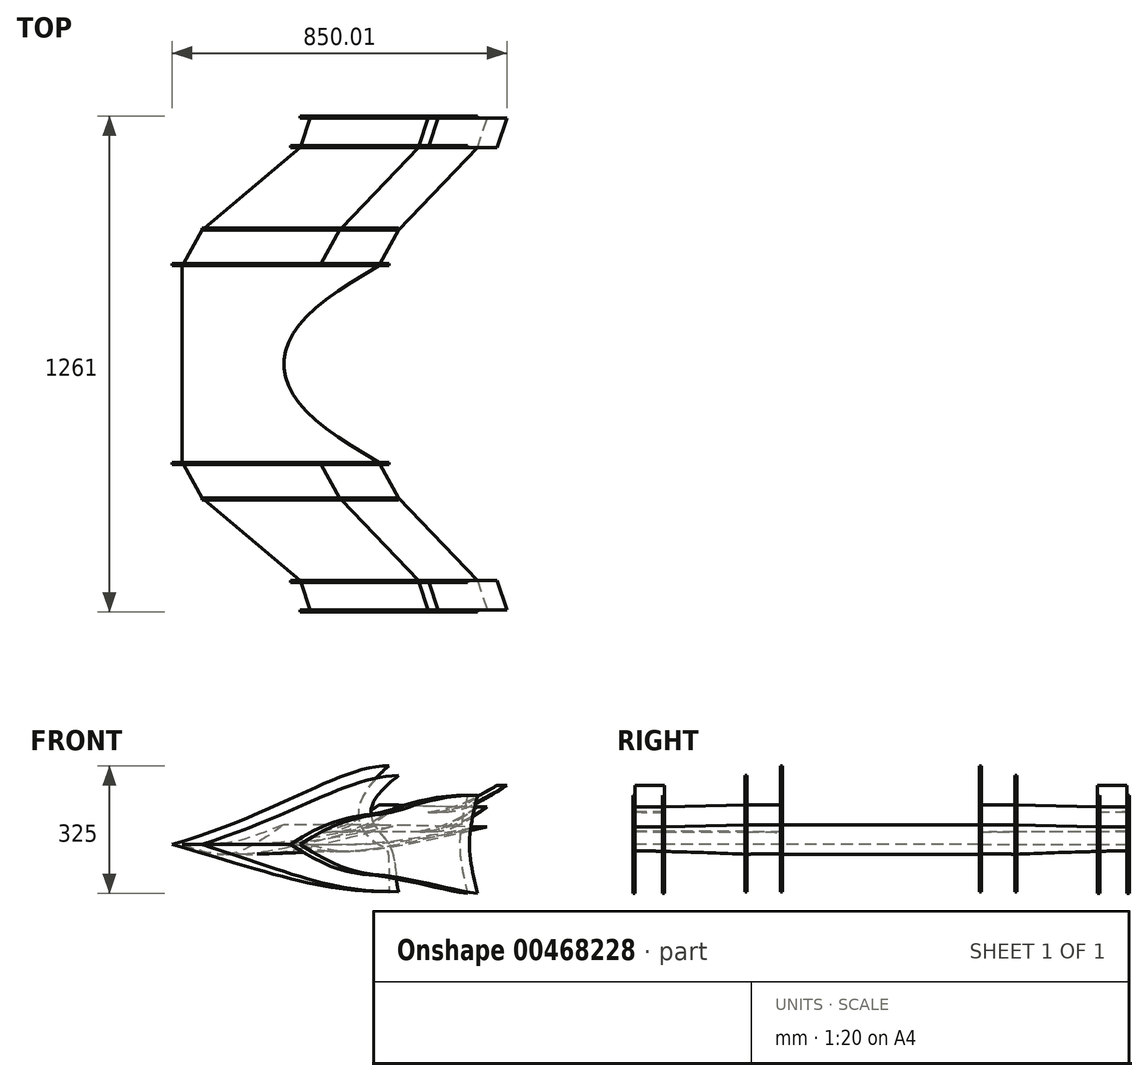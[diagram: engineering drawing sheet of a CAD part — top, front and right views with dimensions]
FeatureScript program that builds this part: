
annotation { "Feature Type Name" : "Feature", "Feature Type Description" : "" }
export const myFeature = defineFeature(function(context is Context, id is Id, definition is map)
    precondition{}
    {
        {
            var Q0;
            Q0=qCreatedBy(makeId("Right.planeOp"),FACE);
            cPlane(context, id + "F0", {"entities" : qUnion([Q0]), "cplaneType" : CPlaneType.OFFSET, "offset" : 250 * mm, "width" : 150 * mm, "height" : 150 * mm});
        }
        {
            var Q0;
            Q0=qCreatedBy(id+"F0.planeOp",FACE);
            var sketch = newSketch(context, id + "F1", { "sketchPlane" : qUnion([Q0])});
            skPoint(sketch, "E0.middle", {"position": v(0, 0) * mm});
            skFitSpline(sketch, "E1", {"points": [v(-275, 0) * mm, v(275, 200) * mm], "startDerivative": vector(825, 240) * mm, "endDerivative": vector(375, 0) * mm});
            skFitSpline(sketch, "E2", {"points": [v(275, 200) * mm, v(250, 0) * mm, v(275, -120) * mm], "startDerivative": vector(-734.18, -640.74) * mm, "endDerivative": vector(0, -821.63) * mm});
            skFitSpline(sketch, "E3", {"points": [v(-275, 0) * mm, v(275, -120) * mm], "startDerivative": vector(825, -240) * mm, "endDerivative": vector(525, 0) * mm});
            skSolve(sketch);
        }
        {
            var Q0;
            Q0=qCreatedBy(makeId("Right.planeOp"),FACE);
            cPlane(context, id + "F2", {"entities" : qUnion([Q0]), "cplaneType" : CPlaneType.OFFSET, "offset" : 340 * mm, "width" : 150 * mm, "height" : 150 * mm});
        }
        {
            var Q0;
            Q0=qCreatedBy(id+"F2.planeOp",FACE);
            var sketch = newSketch(context, id + "F3", { "sketchPlane" : qUnion([Q0])});
            skFitSpline(sketch, "E4", {"points": [v(-200, 0) * mm, v(300, 175) * mm], "startDerivative": vector(750, 240) * mm, "endDerivative": vector(375, 0) * mm});
            skFitSpline(sketch, "E5", {"points": [v(300, 175) * mm, v(275, 0) * mm, v(300, -120) * mm], "startDerivative": vector(-687.26, -522.32) * mm, "endDerivative": vector(77.93, -251.25) * mm});
            skFitSpline(sketch, "E6", {"points": [v(-200, 0) * mm, v(300, -120) * mm], "startDerivative": vector(750, -240) * mm, "endDerivative": vector(525, 0) * mm});
            skSolve(sketch);
        }
        {
            var Q0;
            Q0=qCreatedBy(makeId("Right.planeOp"),FACE);
            cPlane(context, id + "F4", {"entities" : qUnion([Q0]), "cplaneType" : CPlaneType.OFFSET, "offset" : 550 * mm, "width" : 150 * mm, "height" : 150 * mm});
        }
        {
            var Q0;
            Q0=qCreatedBy(id+"F4.planeOp",FACE);
            var sketch = newSketch(context, id + "F5", { "sketchPlane" : qUnion([Q0])});
            skFitSpline(sketch, "E7", {"points": [v(25, 0) * mm, v(250, 80) * mm, v(475, 125) * mm], "startDerivative": vector(742.6, 475.26) * mm, "endDerivative": vector(681.8, 0) * mm});
            skFitSpline(sketch, "E8", {"points": [v(475, 125) * mm, v(455, 0) * mm, v(475, -125) * mm], "startDerivative": vector(-60, -250) * mm, "endDerivative": vector(60, -250) * mm});
            skFitSpline(sketch, "E9", {"points": [v(25, 0) * mm, v(250, -80) * mm, v(475, -125) * mm], "startDerivative": vector(742.6, -475.26) * mm, "endDerivative": vector(456.76, -74.2) * mm});
            skSolve(sketch);
        }
        {
            var Q0;
            Q0=qCreatedBy(makeId("Right.planeOp"),FACE);
            cPlane(context, id + "F6", {"entities" : qUnion([Q0]), "cplaneType" : CPlaneType.OFFSET, "offset" : 625 * mm, "width" : 150 * mm, "height" : 150 * mm});
        }
        {
            var Q0;
            Q0=qCreatedBy(id+"F6.planeOp",FACE);
            var sketch = newSketch(context, id + "F7", { "sketchPlane" : qUnion([Q0])});
            skFitSpline(sketch, "E10", {"points": [v(50, 0) * mm, v(275, 80) * mm, v(500, 125) * mm], "startDerivative": vector(742.6, 475.26) * mm, "endDerivative": vector(681.8, 0) * mm});
            skFitSpline(sketch, "E11", {"points": [v(500, 125) * mm, v(480, 0) * mm, v(500, -125) * mm], "startDerivative": vector(-60, -250) * mm, "endDerivative": vector(60, -250) * mm});
            skFitSpline(sketch, "E12", {"points": [v(50, 0) * mm, v(275, -80) * mm, v(500, -125) * mm], "startDerivative": vector(742.6, -475.26) * mm, "endDerivative": vector(456.76, -74.2) * mm});
            skSolve(sketch);
        }
        {
            var Q0;
            Q0=qCreatedBy(makeId("Right.planeOp"),FACE);
            cPlane(context, id + "F8", {"entities" : qUnion([Q0]), "cplaneType" : CPlaneType.OFFSET, "offset" : 160 * mm, "width" : 150 * mm, "height" : 150 * mm});
        }
        {
            var Q0;
            Q0=qCreatedBy(id+"F8.planeOp",FACE);
            var sketch = newSketch(context, id + "F9", { "sketchPlane" : qUnion([Q0])});
            skFitSpline(sketch, "E13", {"points": [v(-250, 0) * mm, v(-125, -25) * mm, v(110, 50) * mm], "startDerivative": vector(276.92, -99.23) * mm, "endDerivative": vector(434.5, 183.8) * mm});
            skFitSpline(sketch, "E14", {"points": [v(-250, 0) * mm, v(110, 50) * mm], "startDerivative": vector(540, 0) * mm, "endDerivative": vector(540, 150) * mm});
            skSolve(sketch);
        }
        {
            var Q0;
            Q0=qCreatedBy(makeId("Right.planeOp"),FACE);
            cPlane(context, id + "F10", {"entities" : qUnion([Q0]), "cplaneType" : CPlaneType.OFFSET, "offset" : 250 * mm, "width" : 150 * mm, "height" : 150 * mm});
        }
        {
            var Q0;
            Q0=qCreatedBy(id+"F10.planeOp",FACE);
            var sketch = newSketch(context, id + "F11", { "sketchPlane" : qUnion([Q0])});
            skFitSpline(sketch, "E15", {"points": [v(-250, 0) * mm, v(-125, -25) * mm, v(250, 50) * mm], "startDerivative": vector(295.75, -102.45) * mm, "endDerivative": vector(670.75, 177.45) * mm});
            skFitSpline(sketch, "E16", {"points": [v(-250, 0) * mm, v(250, 50) * mm], "startDerivative": vector(750, 0) * mm, "endDerivative": vector(750, 150) * mm});
            skSolve(sketch);
        }
        {
            var Q0;
            Q0=qCreatedBy(id+"F10.planeOp",FACE);
            var sketch = newSketch(context, id + "F12", { "sketchPlane" : qUnion([Q0])});
            skFitSpline(sketch, "E17", {"points": [v(100, 32) * mm, v(125, 32) * mm, v(250, 100) * mm], "startDerivative": vector(70.95, -14.25) * mm, "endDerivative": vector(319.3, 251.19) * mm});
            skFitSpline(sketch, "E18", {"points": [v(100, 32) * mm, v(250, 100) * mm], "startDerivative": vector(225, 54) * mm, "endDerivative": vector(225, 150) * mm});
            skSolve(sketch);
        }
        {
            var Q0;
            Q0=qCreatedBy(makeId("Right.planeOp"),FACE);
            cPlane(context, id + "F13", {"entities" : qUnion([Q0]), "cplaneType" : CPlaneType.OFFSET, "offset" : 340 * mm, "width" : 150 * mm, "height" : 150 * mm});
        }
        {
            var Q0;
            Q0=qCreatedBy(id+"F13.planeOp",FACE);
            var sketch = newSketch(context, id + "F14", { "sketchPlane" : qUnion([Q0])});
            skFitSpline(sketch, "E19", {"points": [v(-200, 0) * mm, v(-75, -25) * mm, v(300, 50) * mm], "startDerivative": vector(295.75, -102.45) * mm, "endDerivative": vector(670.75, 177.45) * mm});
            skFitSpline(sketch, "E20", {"points": [v(-200, 0) * mm, v(300, 50) * mm], "startDerivative": vector(750, 0) * mm, "endDerivative": vector(750, 150) * mm});
            skSolve(sketch);
        }
        {
            var Q0;
            Q0=qCreatedBy(id+"F13.planeOp",FACE);
            var sketch = newSketch(context, id + "F15", { "sketchPlane" : qUnion([Q0])});
            skFitSpline(sketch, "E21", {"points": [v(150, 32.5) * mm, v(175, 32.5) * mm, v(300, 100) * mm], "startDerivative": vector(70.88, -14.16) * mm, "endDerivative": vector(319.39, 250.19) * mm});
            skFitSpline(sketch, "E22", {"points": [v(150, 32.5) * mm, v(300, 100) * mm], "startDerivative": vector(225, 52.5) * mm, "endDerivative": vector(225, 150) * mm});
            skSolve(sketch);
        }
        {
            var Q0;
            Q0=qCreatedBy(makeId("Right.planeOp"),FACE);
            cPlane(context, id + "F16", {"entities" : qUnion([Q0]), "cplaneType" : CPlaneType.OFFSET, "offset" : 550 * mm, "width" : 150 * mm, "height" : 150 * mm});
        }
        {
            var Q0;
            Q0=qCreatedBy(id+"F16.planeOp",FACE);
            var sketch = newSketch(context, id + "F17", { "sketchPlane" : qUnion([Q0])});
            skFitSpline(sketch, "E23", {"points": [v(50, 0) * mm, v(150, -18) * mm, v(500, 45) * mm], "startDerivative": vector(243.54, -77.51) * mm, "endDerivative": vector(618.54, 145.01) * mm});
            skFitSpline(sketch, "E24", {"points": [v(50, 0) * mm, v(500, 45) * mm], "startDerivative": vector(600, 0) * mm, "endDerivative": vector(750, 135) * mm});
            skSolve(sketch);
        }
        {
            var Q0;
            Q0=qCreatedBy(id+"F16.planeOp",FACE);
            var sketch = newSketch(context, id + "F18", { "sketchPlane" : qUnion([Q0])});
            skFitSpline(sketch, "E25", {"points": [v(350, 33) * mm, v(375, 33) * mm, v(500, 95) * mm], "startDerivative": vector(70.1, -13.12) * mm, "endDerivative": vector(320.24, 228.44) * mm});
            skFitSpline(sketch, "E26", {"points": [v(350, 33) * mm, v(500, 95) * mm], "startDerivative": vector(225, 51) * mm, "endDerivative": vector(225, 135) * mm});
            skSolve(sketch);
        }
        {
            var Q0;
            Q0=qCreatedBy(id+"F16.planeOp",FACE);
            var sketch = newSketch(context, id + "F19", { "sketchPlane" : qUnion([Q0])});
            skFitSpline(sketch, "E27", {"points": [v(375, 82) * mm, v(400, 82) * mm, v(550, 150) * mm], "startDerivative": vector(72.45, -13.25) * mm, "endDerivative": vector(364.77, 245.96) * mm});
            skFitSpline(sketch, "E28", {"points": [v(375, 82) * mm, v(550, 150) * mm], "startDerivative": vector(262.5, 54) * mm, "endDerivative": vector(262.5, 150) * mm});
            skSolve(sketch);
        }
        {
            var Q0;
            Q0=qCreatedBy(makeId("Right.planeOp"),FACE);
            cPlane(context, id + "F20", {"entities" : qUnion([Q0]), "cplaneType" : CPlaneType.OFFSET, "offset" : 625 * mm, "width" : 150 * mm, "height" : 150 * mm});
        }
        {
            var Q0;
            Q0=qCreatedBy(id+"F20.planeOp",FACE);
            var sketch = newSketch(context, id + "F21", { "sketchPlane" : qUnion([Q0])});
            skFitSpline(sketch, "E29", {"points": [v(75, 0) * mm, v(175, -17) * mm, v(525, 45) * mm], "startDerivative": vector(243.71, -73.88) * mm, "endDerivative": vector(618.37, 142.03) * mm});
            skFitSpline(sketch, "E30", {"points": [v(75, 0) * mm, v(525, 45) * mm], "startDerivative": vector(600, 0) * mm, "endDerivative": vector(750, 135) * mm});
            skSolve(sketch);
        }
        {
            var Q0;
            Q0=qCreatedBy(id+"F20.planeOp",FACE);
            var sketch = newSketch(context, id + "F22", { "sketchPlane" : qUnion([Q0])});
            skFitSpline(sketch, "E31", {"points": [v(375, 33.5) * mm, v(400, 33.5) * mm, v(525, 95) * mm], "startDerivative": vector(70.04, -13.03) * mm, "endDerivative": vector(320.32, 227.42) * mm});
            skFitSpline(sketch, "E32", {"points": [v(375, 33.5) * mm, v(525, 95) * mm], "startDerivative": vector(225, 49.5) * mm, "endDerivative": vector(225, 135) * mm});
            skSolve(sketch);
        }
        {
            var Q0;
            Q0=qCreatedBy(id+"F20.planeOp",FACE);
            var sketch = newSketch(context, id + "F23", { "sketchPlane" : qUnion([Q0])});
            skFitSpline(sketch, "E33", {"points": [v(400, 83) * mm, v(425, 83) * mm, v(575, 150) * mm], "startDerivative": vector(72.33, -13.07) * mm, "endDerivative": vector(364.9, 243.96) * mm});
            skFitSpline(sketch, "E34", {"points": [v(400, 83) * mm, v(575, 150) * mm], "startDerivative": vector(262.5, 51) * mm, "endDerivative": vector(262.5, 150) * mm});
            skSolve(sketch);
        }
        {
            var Q0;
            Q0=qCreatedBy(makeId("Right.planeOp"),FACE);
            cPlane(context, id + "F24", {"entities" : qUnion([Q0]), "cplaneType" : CPlaneType.OFFSET, "offset" : 250 * mm, "oppositeDirection" : true, "width" : 150 * mm, "height" : 150 * mm});
        }
        {
            var Q0;
            Q0=qCreatedBy(id+"F24.planeOp",FACE);
            var sketch = newSketch(context, id + "F25", { "sketchPlane" : qUnion([Q0])});
            skPoint(sketch, "E35.middle", {"position": v(0, 0) * mm});
            skFitSpline(sketch, "E36", {"points": [v(-275, 0) * mm, v(275, 200) * mm], "startDerivative": vector(825, 240) * mm, "endDerivative": vector(375, 0) * mm});
            skFitSpline(sketch, "E37", {"points": [v(275, 200) * mm, v(250, 0) * mm, v(275, -120) * mm], "startDerivative": vector(-734.18, -640.74) * mm, "endDerivative": vector(0, -821.63) * mm});
            skFitSpline(sketch, "E38", {"points": [v(-275, 0) * mm, v(275, -120) * mm], "startDerivative": vector(825, -240) * mm, "endDerivative": vector(525, 0) * mm});
            skSolve(sketch);
        }
        {
            var Q0;
            Q0=qCreatedBy(makeId("Right.planeOp"),FACE);
            cPlane(context, id + "F26", {"entities" : qUnion([Q0]), "cplaneType" : CPlaneType.OFFSET, "offset" : 340 * mm, "oppositeDirection" : true, "width" : 150 * mm, "height" : 150 * mm});
        }
        {
            var Q0;
            Q0=qCreatedBy(id+"F26.planeOp",FACE);
            var sketch = newSketch(context, id + "F27", { "sketchPlane" : qUnion([Q0])});
            skFitSpline(sketch, "E39", {"points": [v(-200, 0) * mm, v(300, 175) * mm], "startDerivative": vector(750, 240) * mm, "endDerivative": vector(375, 0) * mm});
            skFitSpline(sketch, "E40", {"points": [v(300, 175) * mm, v(275, 0) * mm, v(300, -120) * mm], "startDerivative": vector(-687.26, -522.32) * mm, "endDerivative": vector(77.93, -251.25) * mm});
            skFitSpline(sketch, "E41", {"points": [v(-200, 0) * mm, v(300, -120) * mm], "startDerivative": vector(750, -240) * mm, "endDerivative": vector(525, 0) * mm});
            skSolve(sketch);
        }
        {
            var Q0;
            Q0=qCreatedBy(makeId("Right.planeOp"),FACE);
            cPlane(context, id + "F28", {"entities" : qUnion([Q0]), "cplaneType" : CPlaneType.OFFSET, "offset" : 550 * mm, "oppositeDirection" : true, "width" : 150 * mm, "height" : 150 * mm});
        }
        {
            var Q0;
            Q0=qCreatedBy(id+"F28.planeOp",FACE);
            var sketch = newSketch(context, id + "F29", { "sketchPlane" : qUnion([Q0])});
            skFitSpline(sketch, "E42", {"points": [v(25, 0) * mm, v(250, 80) * mm, v(475, 125) * mm], "startDerivative": vector(742.6, 475.26) * mm, "endDerivative": vector(681.8, 0) * mm});
            skFitSpline(sketch, "E43", {"points": [v(475, 125) * mm, v(455, 0) * mm, v(475, -125) * mm], "startDerivative": vector(-60, -250) * mm, "endDerivative": vector(60, -250) * mm});
            skFitSpline(sketch, "E44", {"points": [v(25, 0) * mm, v(250, -80) * mm, v(475, -125) * mm], "startDerivative": vector(742.6, -475.26) * mm, "endDerivative": vector(456.76, -74.2) * mm});
            skSolve(sketch);
        }
        {
            var Q0;
            Q0=qCreatedBy(makeId("Right.planeOp"),FACE);
            cPlane(context, id + "F30", {"entities" : qUnion([Q0]), "cplaneType" : CPlaneType.OFFSET, "offset" : 625 * mm, "oppositeDirection" : true, "width" : 150 * mm, "height" : 150 * mm});
        }
        {
            var Q0;
            Q0=qCreatedBy(id+"F30.planeOp",FACE);
            var sketch = newSketch(context, id + "F31", { "sketchPlane" : qUnion([Q0])});
            skFitSpline(sketch, "E45", {"points": [v(50, 0) * mm, v(275, 80) * mm, v(500, 125) * mm], "startDerivative": vector(742.6, 475.26) * mm, "endDerivative": vector(681.8, 0) * mm});
            skFitSpline(sketch, "E46", {"points": [v(500, 125) * mm, v(480, 0) * mm, v(500, -125) * mm], "startDerivative": vector(-60, -250) * mm, "endDerivative": vector(60, -250) * mm});
            skFitSpline(sketch, "E47", {"points": [v(50, 0) * mm, v(275, -80) * mm, v(500, -125) * mm], "startDerivative": vector(742.6, -475.26) * mm, "endDerivative": vector(456.76, -74.2) * mm});
            skSolve(sketch);
        }
        {
            var Q0;
            Q0=qCreatedBy(makeId("Right.planeOp"),FACE);
            cPlane(context, id + "F32", {"entities" : qUnion([Q0]), "cplaneType" : CPlaneType.OFFSET, "offset" : 160 * mm, "oppositeDirection" : true, "width" : 150 * mm, "height" : 150 * mm});
        }
        {
            var Q0;
            Q0=qCreatedBy(id+"F32.planeOp",FACE);
            var sketch = newSketch(context, id + "F33", { "sketchPlane" : qUnion([Q0])});
            skFitSpline(sketch, "E48", {"points": [v(-250, 0) * mm, v(-125, -25) * mm, v(110, 50) * mm], "startDerivative": vector(276.92, -99.23) * mm, "endDerivative": vector(434.5, 183.8) * mm});
            skFitSpline(sketch, "E49", {"points": [v(-250, 0) * mm, v(110, 50) * mm], "startDerivative": vector(540, 0) * mm, "endDerivative": vector(540, 150) * mm});
            skSolve(sketch);
        }
        {
            var Q0;
            Q0=qCreatedBy(makeId("Right.planeOp"),FACE);
            cPlane(context, id + "F34", {"entities" : qUnion([Q0]), "cplaneType" : CPlaneType.OFFSET, "offset" : 250 * mm, "oppositeDirection" : true, "width" : 150 * mm, "height" : 150 * mm});
        }
        {
            var Q0;
            Q0=qCreatedBy(id+"F34.planeOp",FACE);
            var sketch = newSketch(context, id + "F35", { "sketchPlane" : qUnion([Q0])});
            skFitSpline(sketch, "E50", {"points": [v(-250, 0) * mm, v(-125, -25) * mm, v(250, 50) * mm], "startDerivative": vector(295.75, -102.45) * mm, "endDerivative": vector(670.75, 177.45) * mm});
            skFitSpline(sketch, "E51", {"points": [v(-250, 0) * mm, v(250, 50) * mm], "startDerivative": vector(750, 0) * mm, "endDerivative": vector(750, 150) * mm});
            skSolve(sketch);
        }
        {
            var Q0;
            Q0=qCreatedBy(id+"F34.planeOp",FACE);
            var sketch = newSketch(context, id + "F36", { "sketchPlane" : qUnion([Q0])});
            skFitSpline(sketch, "E52", {"points": [v(100, 32) * mm, v(125, 32) * mm, v(250, 100) * mm], "startDerivative": vector(70.95, -14.25) * mm, "endDerivative": vector(319.3, 251.19) * mm});
            skFitSpline(sketch, "E53", {"points": [v(100, 32) * mm, v(250, 100) * mm], "startDerivative": vector(225, 54) * mm, "endDerivative": vector(225, 150) * mm});
            skSolve(sketch);
        }
        {
            var Q0;
            Q0=qCreatedBy(makeId("Right.planeOp"),FACE);
            cPlane(context, id + "F37", {"entities" : qUnion([Q0]), "cplaneType" : CPlaneType.OFFSET, "offset" : 340 * mm, "oppositeDirection" : true, "width" : 150 * mm, "height" : 150 * mm});
        }
        {
            var Q0;
            Q0=qCreatedBy(id+"F37.planeOp",FACE);
            var sketch = newSketch(context, id + "F38", { "sketchPlane" : qUnion([Q0])});
            skFitSpline(sketch, "E54", {"points": [v(-200, 0) * mm, v(-75, -25) * mm, v(300, 50) * mm], "startDerivative": vector(295.75, -102.45) * mm, "endDerivative": vector(670.75, 177.45) * mm});
            skFitSpline(sketch, "E55", {"points": [v(-200, 0) * mm, v(300, 50) * mm], "startDerivative": vector(750, 0) * mm, "endDerivative": vector(750, 150) * mm});
            skSolve(sketch);
        }
        {
            var Q0;
            Q0=qCreatedBy(id+"F37.planeOp",FACE);
            var sketch = newSketch(context, id + "F39", { "sketchPlane" : qUnion([Q0])});
            skFitSpline(sketch, "E56", {"points": [v(150, 32.5) * mm, v(175, 32.5) * mm, v(300, 100) * mm], "startDerivative": vector(70.88, -14.16) * mm, "endDerivative": vector(319.39, 250.19) * mm});
            skFitSpline(sketch, "E57", {"points": [v(150, 32.5) * mm, v(300, 100) * mm], "startDerivative": vector(225, 52.5) * mm, "endDerivative": vector(225, 150) * mm});
            skSolve(sketch);
        }
        {
            var Q0;
            Q0=qCreatedBy(makeId("Right.planeOp"),FACE);
            cPlane(context, id + "F40", {"entities" : qUnion([Q0]), "cplaneType" : CPlaneType.OFFSET, "offset" : 550 * mm, "oppositeDirection" : true, "width" : 150 * mm, "height" : 150 * mm});
        }
        {
            var Q0;
            Q0=qCreatedBy(id+"F40.planeOp",FACE);
            var sketch = newSketch(context, id + "F41", { "sketchPlane" : qUnion([Q0])});
            skFitSpline(sketch, "E58", {"points": [v(50, 0) * mm, v(150, -18) * mm, v(500, 45) * mm], "startDerivative": vector(243.54, -77.51) * mm, "endDerivative": vector(618.54, 145.01) * mm});
            skFitSpline(sketch, "E59", {"points": [v(50, 0) * mm, v(500, 45) * mm], "startDerivative": vector(600, 0) * mm, "endDerivative": vector(750, 135) * mm});
            skSolve(sketch);
        }
        {
            var Q0;
            Q0=qCreatedBy(id+"F40.planeOp",FACE);
            var sketch = newSketch(context, id + "F42", { "sketchPlane" : qUnion([Q0])});
            skFitSpline(sketch, "E60", {"points": [v(350, 33) * mm, v(375, 33) * mm, v(500, 95) * mm], "startDerivative": vector(70.1, -13.12) * mm, "endDerivative": vector(320.24, 228.44) * mm});
            skFitSpline(sketch, "E61", {"points": [v(350, 33) * mm, v(500, 95) * mm], "startDerivative": vector(225, 51) * mm, "endDerivative": vector(225, 135) * mm});
            skSolve(sketch);
        }
        {
            var Q0;
            Q0=qCreatedBy(id+"F40.planeOp",FACE);
            var sketch = newSketch(context, id + "F43", { "sketchPlane" : qUnion([Q0])});
            skFitSpline(sketch, "E62", {"points": [v(375, 82) * mm, v(400, 82) * mm, v(550, 150) * mm], "startDerivative": vector(72.45, -13.25) * mm, "endDerivative": vector(364.77, 245.96) * mm});
            skFitSpline(sketch, "E63", {"points": [v(375, 82) * mm, v(550, 150) * mm], "startDerivative": vector(262.5, 54) * mm, "endDerivative": vector(262.5, 150) * mm});
            skSolve(sketch);
        }
        {
            var Q0;
            Q0=qCreatedBy(makeId("Right.planeOp"),FACE);
            cPlane(context, id + "F44", {"entities" : qUnion([Q0]), "cplaneType" : CPlaneType.OFFSET, "offset" : 625 * mm, "oppositeDirection" : true, "width" : 150 * mm, "height" : 150 * mm});
        }
        {
            var Q0;
            Q0=qCreatedBy(id+"F44.planeOp",FACE);
            var sketch = newSketch(context, id + "F45", { "sketchPlane" : qUnion([Q0])});
            skFitSpline(sketch, "E64", {"points": [v(75, 0) * mm, v(175, -17) * mm, v(525, 45) * mm], "startDerivative": vector(243.71, -73.88) * mm, "endDerivative": vector(618.37, 142.03) * mm});
            skFitSpline(sketch, "E65", {"points": [v(75, 0) * mm, v(525, 45) * mm], "startDerivative": vector(600, 0) * mm, "endDerivative": vector(750, 135) * mm});
            skSolve(sketch);
        }
        {
            var Q0;
            Q0=qCreatedBy(id+"F44.planeOp",FACE);
            var sketch = newSketch(context, id + "F46", { "sketchPlane" : qUnion([Q0])});
            skFitSpline(sketch, "E66", {"points": [v(375, 33.5) * mm, v(400, 33.5) * mm, v(525, 95) * mm], "startDerivative": vector(70.04, -13.03) * mm, "endDerivative": vector(320.32, 227.42) * mm});
            skFitSpline(sketch, "E67", {"points": [v(375, 33.5) * mm, v(525, 95) * mm], "startDerivative": vector(225, 49.5) * mm, "endDerivative": vector(225, 135) * mm});
            skSolve(sketch);
        }
        {
            var Q0;
            Q0=qCreatedBy(id+"F44.planeOp",FACE);
            var sketch = newSketch(context, id + "F47", { "sketchPlane" : qUnion([Q0])});
            skFitSpline(sketch, "E68", {"points": [v(400, 83) * mm, v(425, 83) * mm, v(575, 150) * mm], "startDerivative": vector(72.33, -13.07) * mm, "endDerivative": vector(364.9, 243.96) * mm});
            skFitSpline(sketch, "E69", {"points": [v(400, 83) * mm, v(575, 150) * mm], "startDerivative": vector(262.5, 51) * mm, "endDerivative": vector(262.5, 150) * mm});
            skSolve(sketch);
        }
        {
            var Q0;
            Q0=makeQuery(id+"F35.imprint","IMPRINT",FACE,{"disambiguationData":[TD([[makeQuery(id+"F35.imprint","IMPRINT",EDGE,{"derivedFrom":sQuery(id+"F35.wireOp",EDGE,"E50")}),1.0]])]});
            var Q1;
            Q1=makeQuery(id+"F33.imprint","IMPRINT",FACE,{"disambiguationData":[TD([[makeQuery(id+"F33.imprint","IMPRINT",EDGE,{"derivedFrom":sQuery(id+"F33.wireOp",EDGE,"E48")}),1.0]])]});
            var Q2;
            Q2=makeQuery(id+"F9.imprint","IMPRINT",FACE,{"disambiguationData":[TD([[makeQuery(id+"F9.imprint","IMPRINT",EDGE,{"derivedFrom":sQuery(id+"F9.wireOp",EDGE,"E13")}),1.0]])]});
            var Q3;
            Q3=makeQuery(id+"F11.imprint","IMPRINT",FACE,{"disambiguationData":[TD([[makeQuery(id+"F11.imprint","IMPRINT",EDGE,{"derivedFrom":sQuery(id+"F11.wireOp",EDGE,"E15")}),1.0]])]});
            loft(context, id + "F48", {"sheetProfilesArray" : [{ "sheetProfileEntities" : qUnion([Q0]) }, { "sheetProfileEntities" : qUnion([Q1]) }, { "sheetProfileEntities" : qUnion([Q2]) }, { "sheetProfileEntities" : qUnion([Q3]) }]});
        }
        {
            var Q1;
            Q1=makeQuery(id+"F48.opLoft","CAP_FACE",FACE,{"disambiguationData":[OSD([makeQuery(id+"F35.imprint","IMPRINT",FACE,{"disambiguationData":[TD([[makeQuery(id+"F35.imprint","IMPRINT",EDGE,{"derivedFrom":sQuery(id+"F35.wireOp",EDGE,"E50")}),1.0]])]})])],"isStart":true});
            var Q2;
            Q2=makeQuery(id+"F38.imprint","IMPRINT",FACE,{"disambiguationData":[TD([[makeQuery(id+"F38.imprint","IMPRINT",EDGE,{"derivedFrom":sQuery(id+"F38.wireOp",EDGE,"E54")}),1.0]])]});
            loft(context, id + "F49", {"operationType" : NewBodyOperationType.ADD, "sheetProfilesArray" : [{ "sheetProfileEntities" : qUnion([Q1]) }, { "sheetProfileEntities" : qUnion([Q2]) }]});
        }
        {
            var Q1;
            Q1=makeQuery(id+"F48.opLoft","CAP_FACE",FACE,{"disambiguationData":[OSD([makeQuery(id+"F11.imprint","IMPRINT",FACE,{"disambiguationData":[TD([[makeQuery(id+"F11.imprint","IMPRINT",EDGE,{"derivedFrom":sQuery(id+"F11.wireOp",EDGE,"E15")}),1.0]])]})])],"isStart":true});
            var Q2;
            Q2=makeQuery(id+"F14.imprint","IMPRINT",FACE,{"disambiguationData":[TD([[makeQuery(id+"F14.imprint","IMPRINT",EDGE,{"derivedFrom":sQuery(id+"F14.wireOp",EDGE,"E19")}),1.0]])]});
            loft(context, id + "F50", {"operationType" : NewBodyOperationType.ADD, "sheetProfilesArray" : [{ "sheetProfileEntities" : qUnion([Q1]) }, { "sheetProfileEntities" : qUnion([Q2]) }]});
        }
        {
            var Q1;
            Q1=makeQuery(id+"F49.opLoft","CAP_FACE",FACE,{"disambiguationData":[OSD([makeQuery(id+"F38.imprint","IMPRINT",FACE,{"disambiguationData":[TD([[makeQuery(id+"F38.imprint","IMPRINT",EDGE,{"derivedFrom":sQuery(id+"F38.wireOp",EDGE,"E54")}),1.0]])]})])],"isStart":true});
            var Q2;
            Q2=makeQuery(id+"F41.imprint","IMPRINT",FACE,{"disambiguationData":[TD([[makeQuery(id+"F41.imprint","IMPRINT",EDGE,{"derivedFrom":sQuery(id+"F41.wireOp",EDGE,"E58")}),1.0]])]});
            loft(context, id + "F51", {"operationType" : NewBodyOperationType.ADD, "sheetProfilesArray" : [{ "sheetProfileEntities" : qUnion([Q1]) }, { "sheetProfileEntities" : qUnion([Q2]) }]});
        }
        {
            var Q1;
            Q1=makeQuery(id+"F50.opLoft","CAP_FACE",FACE,{"disambiguationData":[OSD([makeQuery(id+"F14.imprint","IMPRINT",FACE,{"disambiguationData":[TD([[makeQuery(id+"F14.imprint","IMPRINT",EDGE,{"derivedFrom":sQuery(id+"F14.wireOp",EDGE,"E19")}),1.0]])]})])],"isStart":true});
            var Q2;
            Q2=makeQuery(id+"F17.imprint","IMPRINT",FACE,{"disambiguationData":[TD([[makeQuery(id+"F17.imprint","IMPRINT",EDGE,{"derivedFrom":sQuery(id+"F17.wireOp",EDGE,"E23")}),1.0]])]});
            loft(context, id + "F52", {"operationType" : NewBodyOperationType.ADD, "sheetProfilesArray" : [{ "sheetProfileEntities" : qUnion([Q1]) }, { "sheetProfileEntities" : qUnion([Q2]) }]});
        }
        {
            var Q1;
            Q1=makeQuery(id+"F51.opLoft","CAP_FACE",FACE,{"disambiguationData":[OSD([makeQuery(id+"F41.imprint","IMPRINT",FACE,{"disambiguationData":[TD([[makeQuery(id+"F41.imprint","IMPRINT",EDGE,{"derivedFrom":sQuery(id+"F41.wireOp",EDGE,"E58")}),1.0]])]})])],"isStart":true});
            var Q2;
            Q2=makeQuery(id+"F45.imprint","IMPRINT",FACE,{"disambiguationData":[TD([[makeQuery(id+"F45.imprint","IMPRINT",EDGE,{"derivedFrom":sQuery(id+"F45.wireOp",EDGE,"E64")}),1.0]])]});
            loft(context, id + "F53", {"operationType" : NewBodyOperationType.ADD, "sheetProfilesArray" : [{ "sheetProfileEntities" : qUnion([Q1]) }, { "sheetProfileEntities" : qUnion([Q2]) }]});
        }
        {
            var Q1;
            Q1=makeQuery(id+"F52.opLoft","CAP_FACE",FACE,{"disambiguationData":[OSD([makeQuery(id+"F17.imprint","IMPRINT",FACE,{"disambiguationData":[TD([[makeQuery(id+"F17.imprint","IMPRINT",EDGE,{"derivedFrom":sQuery(id+"F17.wireOp",EDGE,"E23")}),1.0]])]})])],"isStart":true});
            var Q2;
            Q2=makeQuery(id+"F21.imprint","IMPRINT",FACE,{"disambiguationData":[TD([[makeQuery(id+"F21.imprint","IMPRINT",EDGE,{"derivedFrom":sQuery(id+"F21.wireOp",EDGE,"E29")}),1.0]])]});
            loft(context, id + "F54", {"operationType" : NewBodyOperationType.ADD, "sheetProfilesArray" : [{ "sheetProfileEntities" : qUnion([Q1]) }, { "sheetProfileEntities" : qUnion([Q2]) }]});
        }
        {
            var Q0;
            Q0=makeQuery(id+"F36.imprint","IMPRINT",FACE,{"disambiguationData":[TD([[makeQuery(id+"F36.imprint","IMPRINT",EDGE,{"derivedFrom":sQuery(id+"F36.wireOp",EDGE,"E52")}),1.0]])]});
            var Q1;
            Q1=makeQuery(id+"F39.imprint","IMPRINT",FACE,{"disambiguationData":[TD([[makeQuery(id+"F39.imprint","IMPRINT",EDGE,{"derivedFrom":sQuery(id+"F39.wireOp",EDGE,"E56")}),1.0]])]});
            loft(context, id + "F55", {"sheetProfilesArray" : [{ "sheetProfileEntities" : qUnion([Q0]) }, { "sheetProfileEntities" : qUnion([Q1]) }]});
        }
        {
            var Q0;
            Q0=makeQuery(id+"F12.imprint","IMPRINT",FACE,{"disambiguationData":[TD([[makeQuery(id+"F12.imprint","IMPRINT",EDGE,{"derivedFrom":sQuery(id+"F12.wireOp",EDGE,"E17")}),1.0]])]});
            var Q1;
            Q1=makeQuery(id+"F15.imprint","IMPRINT",FACE,{"disambiguationData":[TD([[makeQuery(id+"F15.imprint","IMPRINT",EDGE,{"derivedFrom":sQuery(id+"F15.wireOp",EDGE,"E21")}),1.0]])]});
            loft(context, id + "F56", {"sheetProfilesArray" : [{ "sheetProfileEntities" : qUnion([Q0]) }, { "sheetProfileEntities" : qUnion([Q1]) }]});
        }
        {
            var Q1;
            Q1=makeQuery(id+"F55.opLoft","CAP_FACE",FACE,{"disambiguationData":[OSD([makeQuery(id+"F39.imprint","IMPRINT",FACE,{"disambiguationData":[TD([[makeQuery(id+"F39.imprint","IMPRINT",EDGE,{"derivedFrom":sQuery(id+"F39.wireOp",EDGE,"E56")}),1.0]])]})])],"isStart":true});
            var Q2;
            Q2=makeQuery(id+"F42.imprint","IMPRINT",FACE,{"disambiguationData":[TD([[makeQuery(id+"F42.imprint","IMPRINT",EDGE,{"derivedFrom":sQuery(id+"F42.wireOp",EDGE,"E60")}),1.0]])]});
            loft(context, id + "F57", {"operationType" : NewBodyOperationType.ADD, "sheetProfilesArray" : [{ "sheetProfileEntities" : qUnion([Q1]) }, { "sheetProfileEntities" : qUnion([Q2]) }]});
        }
        {
            var Q1;
            Q1=makeQuery(id+"F56.opLoft","CAP_FACE",FACE,{"disambiguationData":[OSD([makeQuery(id+"F15.imprint","IMPRINT",FACE,{"disambiguationData":[TD([[makeQuery(id+"F15.imprint","IMPRINT",EDGE,{"derivedFrom":sQuery(id+"F15.wireOp",EDGE,"E21")}),1.0]])]})])],"isStart":true});
            var Q2;
            Q2=makeQuery(id+"F18.imprint","IMPRINT",FACE,{"disambiguationData":[TD([[makeQuery(id+"F18.imprint","IMPRINT",EDGE,{"derivedFrom":sQuery(id+"F18.wireOp",EDGE,"E25")}),1.0]])]});
            loft(context, id + "F58", {"operationType" : NewBodyOperationType.ADD, "sheetProfilesArray" : [{ "sheetProfileEntities" : qUnion([Q1]) }, { "sheetProfileEntities" : qUnion([Q2]) }]});
        }
        {
            var Q1;
            Q1=makeQuery(id+"F57.opLoft","CAP_FACE",FACE,{"disambiguationData":[OSD([makeQuery(id+"F42.imprint","IMPRINT",FACE,{"disambiguationData":[TD([[makeQuery(id+"F42.imprint","IMPRINT",EDGE,{"derivedFrom":sQuery(id+"F42.wireOp",EDGE,"E60")}),1.0]])]})])],"isStart":true});
            var Q2;
            Q2=makeQuery(id+"F46.imprint","IMPRINT",FACE,{"disambiguationData":[TD([[makeQuery(id+"F46.imprint","IMPRINT",EDGE,{"derivedFrom":sQuery(id+"F46.wireOp",EDGE,"E66")}),1.0]])]});
            loft(context, id + "F59", {"operationType" : NewBodyOperationType.ADD, "sheetProfilesArray" : [{ "sheetProfileEntities" : qUnion([Q1]) }, { "sheetProfileEntities" : qUnion([Q2]) }]});
        }
        {
            var Q1;
            Q1=makeQuery(id+"F58.opLoft","CAP_FACE",FACE,{"disambiguationData":[OSD([makeQuery(id+"F18.imprint","IMPRINT",FACE,{"disambiguationData":[TD([[makeQuery(id+"F18.imprint","IMPRINT",EDGE,{"derivedFrom":sQuery(id+"F18.wireOp",EDGE,"E25")}),1.0]])]})])],"isStart":true});
            var Q2;
            Q2=makeQuery(id+"F22.imprint","IMPRINT",FACE,{"disambiguationData":[TD([[makeQuery(id+"F22.imprint","IMPRINT",EDGE,{"derivedFrom":sQuery(id+"F22.wireOp",EDGE,"E31")}),1.0]])]});
            loft(context, id + "F60", {"operationType" : NewBodyOperationType.ADD, "sheetProfilesArray" : [{ "sheetProfileEntities" : qUnion([Q1]) }, { "sheetProfileEntities" : qUnion([Q2]) }]});
        }
        {
            var Q0;
            Q0=makeQuery(id+"F43.imprint","IMPRINT",FACE,{"disambiguationData":[TD([[makeQuery(id+"F43.imprint","IMPRINT",EDGE,{"derivedFrom":sQuery(id+"F43.wireOp",EDGE,"E62")}),1.0]])]});
            var Q1;
            Q1=makeQuery(id+"F47.imprint","IMPRINT",FACE,{"disambiguationData":[TD([[makeQuery(id+"F47.imprint","IMPRINT",EDGE,{"derivedFrom":sQuery(id+"F47.wireOp",EDGE,"E68")}),1.0]])]});
            loft(context, id + "F61", {"sheetProfilesArray" : [{ "sheetProfileEntities" : qUnion([Q0]) }, { "sheetProfileEntities" : qUnion([Q1]) }]});
        }
        {
            var Q0;
            Q0=makeQuery(id+"F19.imprint","IMPRINT",FACE,{"disambiguationData":[TD([[makeQuery(id+"F19.imprint","IMPRINT",EDGE,{"derivedFrom":sQuery(id+"F19.wireOp",EDGE,"E27")}),1.0]])]});
            var Q1;
            Q1=makeQuery(id+"F23.imprint","IMPRINT",FACE,{"disambiguationData":[TD([[makeQuery(id+"F23.imprint","IMPRINT",EDGE,{"derivedFrom":sQuery(id+"F23.wireOp",EDGE,"E33")}),1.0]])]});
            loft(context, id + "F62", {"sheetProfilesArray" : [{ "sheetProfileEntities" : qUnion([Q0]) }, { "sheetProfileEntities" : qUnion([Q1]) }]});
        }
        {
            var Q0;
            Q0=makeQuery(id+"F25.imprint","IMPRINT",FACE,{"disambiguationData":[TD([[makeQuery(id+"F25.imprint","IMPRINT",EDGE,{"derivedFrom":sQuery(id+"F25.wireOp",EDGE,"E36")}),-1.0]])]});
            extrude(context, id + "F63", {"entities" : qUnion([Q0]), "oppositeDirection" : true, "depth" : 5.5 * mm});
        }
        {
            var Q0;
            Q0=makeQuery(id+"F1.imprint","IMPRINT",FACE,{"disambiguationData":[TD([[makeQuery(id+"F1.imprint","IMPRINT",EDGE,{"derivedFrom":sQuery(id+"F1.wireOp",EDGE,"E1")}),-1.0]])]});
            extrude(context, id + "F64", {"entities" : qUnion([Q0]), "depth" : 5.5 * mm});
        }
        {
            var Q0;
            Q0=makeQuery(id+"F27.imprint","IMPRINT",FACE,{"disambiguationData":[TD([[makeQuery(id+"F27.imprint","IMPRINT",EDGE,{"derivedFrom":sQuery(id+"F27.wireOp",EDGE,"E39")}),-1.0]])]});
            extrude(context, id + "F65", {"entities" : qUnion([Q0]), "oppositeDirection" : true, "depth" : 5.5 * mm});
        }
        {
            var Q0;
            Q0=makeQuery(id+"F3.imprint","IMPRINT",FACE,{"disambiguationData":[TD([[makeQuery(id+"F3.imprint","IMPRINT",EDGE,{"derivedFrom":sQuery(id+"F3.wireOp",EDGE,"E4")}),-1.0]])]});
            extrude(context, id + "F66", {"entities" : qUnion([Q0]), "depth" : 5.5 * mm});
        }
        {
            var Q0;
            Q0=makeQuery(id+"F29.imprint","IMPRINT",FACE,{"disambiguationData":[TD([[makeQuery(id+"F29.imprint","IMPRINT",EDGE,{"derivedFrom":sQuery(id+"F29.wireOp",EDGE,"E42")}),-1.0]])]});
            extrude(context, id + "F67", {"entities" : qUnion([Q0]), "oppositeDirection" : true, "depth" : 5.5 * mm});
        }
        {
            var Q0;
            Q0=makeQuery(id+"F5.imprint","IMPRINT",FACE,{"disambiguationData":[TD([[makeQuery(id+"F5.imprint","IMPRINT",EDGE,{"derivedFrom":sQuery(id+"F5.wireOp",EDGE,"E7")}),-1.0]])]});
            extrude(context, id + "F68", {"entities" : qUnion([Q0]), "depth" : 5.5 * mm});
        }
        {
            var Q0;
            Q0=makeQuery(id+"F31.imprint","IMPRINT",FACE,{"disambiguationData":[TD([[makeQuery(id+"F31.imprint","IMPRINT",EDGE,{"derivedFrom":sQuery(id+"F31.wireOp",EDGE,"E45")}),-1.0]])]});
            extrude(context, id + "F69", {"entities" : qUnion([Q0]), "oppositeDirection" : true, "depth" : 5.5 * mm});
        }
        {
            var Q0;
            Q0=makeQuery(id+"F7.imprint","IMPRINT",FACE,{"disambiguationData":[TD([[makeQuery(id+"F7.imprint","IMPRINT",EDGE,{"derivedFrom":sQuery(id+"F7.wireOp",EDGE,"E10")}),-1.0]])]});
            extrude(context, id + "F70", {"entities" : qUnion([Q0]), "depth" : 5.5 * mm});
        }
        {
            var Q0;
            Q0=qCreatedBy(makeId("Right.planeOp"),FACE);
            var sketch = newSketch(context, id + "F71", { "sketchPlane" : qUnion([Q0])});
            skLineSegment(sketch, "E70.bottom", {"start": v(-250, 250) * mm, "end": v(250, 250) * mm});
            skLineSegment(sketch, "E70.top", {"start": v(-250, -250) * mm, "end": v(250, -250) * mm});
            skLineSegment(sketch, "E70.left", {"start": v(-250, 250) * mm, "end": v(-250, -250) * mm});
            skLineSegment(sketch, "E70.right", {"start": v(250, 250) * mm, "end": v(250, -250) * mm});
            skPoint(sketch, "E70.middle", {"position": v(0, 0) * mm});
            skSolve(sketch);
        }
        {
            var Q0;
            Q0=makeQuery(id+"F48.opLoft","SWEPT_BODY",BODY,{"disambiguationData":[OSD([sQuery(id+"F9.wireOp",EDGE,"E14"),makeQuery(id+"F11.imprint","IMPRINT",FACE,{"disambiguationData":[TD([[makeQuery(id+"F11.imprint","IMPRINT",EDGE,{"derivedFrom":sQuery(id+"F11.wireOp",EDGE,"E15")}),1.0]])]}),sQuery(id+"F33.wireOp",EDGE,"E49"),makeQuery(id+"F35.imprint","IMPRINT",FACE,{"disambiguationData":[TD([[makeQuery(id+"F35.imprint","IMPRINT",EDGE,{"derivedFrom":sQuery(id+"F35.wireOp",EDGE,"E50")}),1.0]])]})])]});
            var Q1;
            Q1=makeQuery(id+"F55.opLoft","SWEPT_BODY",BODY,{"disambiguationData":[OSD([makeQuery(id+"F36.imprint","IMPRINT",FACE,{"disambiguationData":[TD([[makeQuery(id+"F36.imprint","IMPRINT",EDGE,{"derivedFrom":sQuery(id+"F36.wireOp",EDGE,"E52")}),1.0]])]}),makeQuery(id+"F39.imprint","IMPRINT",FACE,{"disambiguationData":[TD([[makeQuery(id+"F39.imprint","IMPRINT",EDGE,{"derivedFrom":sQuery(id+"F39.wireOp",EDGE,"E56")}),1.0]])]})])]});
            var Q2;
            Q2=makeQuery(id+"F56.opLoft","SWEPT_BODY",BODY,{"disambiguationData":[OSD([makeQuery(id+"F12.imprint","IMPRINT",FACE,{"disambiguationData":[TD([[makeQuery(id+"F12.imprint","IMPRINT",EDGE,{"derivedFrom":sQuery(id+"F12.wireOp",EDGE,"E17")}),1.0]])]}),makeQuery(id+"F15.imprint","IMPRINT",FACE,{"disambiguationData":[TD([[makeQuery(id+"F15.imprint","IMPRINT",EDGE,{"derivedFrom":sQuery(id+"F15.wireOp",EDGE,"E21")}),1.0]])]})])]});
            var Q3;
            Q3=makeQuery(id+"F61.opLoft","SWEPT_BODY",BODY,{"disambiguationData":[OSD([makeQuery(id+"F43.imprint","IMPRINT",FACE,{"disambiguationData":[TD([[makeQuery(id+"F43.imprint","IMPRINT",EDGE,{"derivedFrom":sQuery(id+"F43.wireOp",EDGE,"E62")}),1.0]])]}),makeQuery(id+"F47.imprint","IMPRINT",FACE,{"disambiguationData":[TD([[makeQuery(id+"F47.imprint","IMPRINT",EDGE,{"derivedFrom":sQuery(id+"F47.wireOp",EDGE,"E68")}),1.0]])]})])]});
            var Q4;
            Q4=makeQuery(id+"F62.opLoft","SWEPT_BODY",BODY,{"disambiguationData":[OSD([makeQuery(id+"F19.imprint","IMPRINT",FACE,{"disambiguationData":[TD([[makeQuery(id+"F19.imprint","IMPRINT",EDGE,{"derivedFrom":sQuery(id+"F19.wireOp",EDGE,"E27")}),1.0]])]}),makeQuery(id+"F23.imprint","IMPRINT",FACE,{"disambiguationData":[TD([[makeQuery(id+"F23.imprint","IMPRINT",EDGE,{"derivedFrom":sQuery(id+"F23.wireOp",EDGE,"E33")}),1.0]])]})])]});
            var Q5;
            Q5=makeQuery(id+"F63.opExtrude","SWEPT_BODY",BODY,{"disambiguationData":[OSD([sQuery(id+"F25.wireOp",EDGE,"E36"),sQuery(id+"F25.wireOp",EDGE,"E37"),sQuery(id+"F25.wireOp",EDGE,"E38")])]});
            var Q6;
            Q6=makeQuery(id+"F64.opExtrude","SWEPT_BODY",BODY,{"disambiguationData":[OSD([sQuery(id+"F1.wireOp",EDGE,"E1"),sQuery(id+"F1.wireOp",EDGE,"E2"),sQuery(id+"F1.wireOp",EDGE,"E3")])]});
            var Q7;
            Q7=makeQuery(id+"F65.opExtrude","SWEPT_BODY",BODY,{"disambiguationData":[OSD([sQuery(id+"F27.wireOp",EDGE,"E39"),sQuery(id+"F27.wireOp",EDGE,"E40"),sQuery(id+"F27.wireOp",EDGE,"E41")])]});
            var Q8;
            Q8=makeQuery(id+"F66.opExtrude","SWEPT_BODY",BODY,{"disambiguationData":[OSD([sQuery(id+"F3.wireOp",EDGE,"E4"),sQuery(id+"F3.wireOp",EDGE,"E5"),sQuery(id+"F3.wireOp",EDGE,"E6")])]});
            var Q9;
            Q9=makeQuery(id+"F67.opExtrude","SWEPT_BODY",BODY,{"disambiguationData":[OSD([sQuery(id+"F29.wireOp",EDGE,"E42"),sQuery(id+"F29.wireOp",EDGE,"E43"),sQuery(id+"F29.wireOp",EDGE,"E44")])]});
            var Q10;
            Q10=makeQuery(id+"F68.opExtrude","SWEPT_BODY",BODY,{"disambiguationData":[OSD([sQuery(id+"F5.wireOp",EDGE,"E7"),sQuery(id+"F5.wireOp",EDGE,"E8"),sQuery(id+"F5.wireOp",EDGE,"E9")])]});
            var Q11;
            Q11=makeQuery(id+"F69.opExtrude","SWEPT_BODY",BODY,{"disambiguationData":[OSD([sQuery(id+"F31.wireOp",EDGE,"E45"),sQuery(id+"F31.wireOp",EDGE,"E46"),sQuery(id+"F31.wireOp",EDGE,"E47")])]});
            var Q12;
            Q12=makeQuery(id+"F70.opExtrude","SWEPT_BODY",BODY,{"disambiguationData":[OSD([sQuery(id+"F7.wireOp",EDGE,"E10"),sQuery(id+"F7.wireOp",EDGE,"E11"),sQuery(id+"F7.wireOp",EDGE,"E12")])]});
            var Q13;
            Q13=sQuery(id+"F71.wireOp",EDGE,"E70.right");
            transform(context, id + "F72", {"entities" : qUnion([Q0, Q1, Q2, Q3, Q4, Q5, Q6, Q7, Q8, Q9, Q10, Q11, Q12]), "transformType" : TransformType.ROTATION, "transformAxis" : qUnion([Q13]), "angle" : 90 * degree, "makeCopy" : false});
        }
        {
            var Q0;
            Q0=makeQuery(id+"F48.opLoft","SWEPT_BODY",BODY,{"disambiguationData":[OSD([sQuery(id+"F9.wireOp",EDGE,"E14"),makeQuery(id+"F11.imprint","IMPRINT",FACE,{"disambiguationData":[TD([[makeQuery(id+"F11.imprint","IMPRINT",EDGE,{"derivedFrom":sQuery(id+"F11.wireOp",EDGE,"E15")}),1.0]])]}),sQuery(id+"F33.wireOp",EDGE,"E49"),makeQuery(id+"F35.imprint","IMPRINT",FACE,{"disambiguationData":[TD([[makeQuery(id+"F35.imprint","IMPRINT",EDGE,{"derivedFrom":sQuery(id+"F35.wireOp",EDGE,"E50")}),1.0]])]})])]});
            var Q1;
            Q1=makeQuery(id+"F55.opLoft","SWEPT_BODY",BODY,{"disambiguationData":[OSD([makeQuery(id+"F36.imprint","IMPRINT",FACE,{"disambiguationData":[TD([[makeQuery(id+"F36.imprint","IMPRINT",EDGE,{"derivedFrom":sQuery(id+"F36.wireOp",EDGE,"E52")}),1.0]])]}),makeQuery(id+"F39.imprint","IMPRINT",FACE,{"disambiguationData":[TD([[makeQuery(id+"F39.imprint","IMPRINT",EDGE,{"derivedFrom":sQuery(id+"F39.wireOp",EDGE,"E56")}),1.0]])]})])]});
            var Q2;
            Q2=makeQuery(id+"F56.opLoft","SWEPT_BODY",BODY,{"disambiguationData":[OSD([makeQuery(id+"F12.imprint","IMPRINT",FACE,{"disambiguationData":[TD([[makeQuery(id+"F12.imprint","IMPRINT",EDGE,{"derivedFrom":sQuery(id+"F12.wireOp",EDGE,"E17")}),1.0]])]}),makeQuery(id+"F15.imprint","IMPRINT",FACE,{"disambiguationData":[TD([[makeQuery(id+"F15.imprint","IMPRINT",EDGE,{"derivedFrom":sQuery(id+"F15.wireOp",EDGE,"E21")}),1.0]])]})])]});
            var Q3;
            Q3=makeQuery(id+"F61.opLoft","SWEPT_BODY",BODY,{"disambiguationData":[OSD([makeQuery(id+"F43.imprint","IMPRINT",FACE,{"disambiguationData":[TD([[makeQuery(id+"F43.imprint","IMPRINT",EDGE,{"derivedFrom":sQuery(id+"F43.wireOp",EDGE,"E62")}),1.0]])]}),makeQuery(id+"F47.imprint","IMPRINT",FACE,{"disambiguationData":[TD([[makeQuery(id+"F47.imprint","IMPRINT",EDGE,{"derivedFrom":sQuery(id+"F47.wireOp",EDGE,"E68")}),1.0]])]})])]});
            var Q4;
            Q4=makeQuery(id+"F62.opLoft","SWEPT_BODY",BODY,{"disambiguationData":[OSD([makeQuery(id+"F19.imprint","IMPRINT",FACE,{"disambiguationData":[TD([[makeQuery(id+"F19.imprint","IMPRINT",EDGE,{"derivedFrom":sQuery(id+"F19.wireOp",EDGE,"E27")}),1.0]])]}),makeQuery(id+"F23.imprint","IMPRINT",FACE,{"disambiguationData":[TD([[makeQuery(id+"F23.imprint","IMPRINT",EDGE,{"derivedFrom":sQuery(id+"F23.wireOp",EDGE,"E33")}),1.0]])]})])]});
            var Q5;
            Q5=makeQuery(id+"F63.opExtrude","SWEPT_BODY",BODY,{"disambiguationData":[OSD([sQuery(id+"F25.wireOp",EDGE,"E36"),sQuery(id+"F25.wireOp",EDGE,"E37"),sQuery(id+"F25.wireOp",EDGE,"E38")])]});
            var Q6;
            Q6=makeQuery(id+"F64.opExtrude","SWEPT_BODY",BODY,{"disambiguationData":[OSD([sQuery(id+"F1.wireOp",EDGE,"E1"),sQuery(id+"F1.wireOp",EDGE,"E2"),sQuery(id+"F1.wireOp",EDGE,"E3")])]});
            var Q7;
            Q7=makeQuery(id+"F65.opExtrude","SWEPT_BODY",BODY,{"disambiguationData":[OSD([sQuery(id+"F27.wireOp",EDGE,"E39"),sQuery(id+"F27.wireOp",EDGE,"E40"),sQuery(id+"F27.wireOp",EDGE,"E41")])]});
            var Q8;
            Q8=makeQuery(id+"F66.opExtrude","SWEPT_BODY",BODY,{"disambiguationData":[OSD([sQuery(id+"F3.wireOp",EDGE,"E4"),sQuery(id+"F3.wireOp",EDGE,"E5"),sQuery(id+"F3.wireOp",EDGE,"E6")])]});
            var Q9;
            Q9=makeQuery(id+"F67.opExtrude","SWEPT_BODY",BODY,{"disambiguationData":[OSD([sQuery(id+"F29.wireOp",EDGE,"E42"),sQuery(id+"F29.wireOp",EDGE,"E43"),sQuery(id+"F29.wireOp",EDGE,"E44")])]});
            var Q10;
            Q10=makeQuery(id+"F68.opExtrude","SWEPT_BODY",BODY,{"disambiguationData":[OSD([sQuery(id+"F5.wireOp",EDGE,"E7"),sQuery(id+"F5.wireOp",EDGE,"E8"),sQuery(id+"F5.wireOp",EDGE,"E9")])]});
            var Q11;
            Q11=makeQuery(id+"F69.opExtrude","SWEPT_BODY",BODY,{"disambiguationData":[OSD([sQuery(id+"F31.wireOp",EDGE,"E45"),sQuery(id+"F31.wireOp",EDGE,"E46"),sQuery(id+"F31.wireOp",EDGE,"E47")])]});
            var Q12;
            Q12=makeQuery(id+"F70.opExtrude","SWEPT_BODY",BODY,{"disambiguationData":[OSD([sQuery(id+"F7.wireOp",EDGE,"E10"),sQuery(id+"F7.wireOp",EDGE,"E11"),sQuery(id+"F7.wireOp",EDGE,"E12")])]});
            transform(context, id + "F73", {"entities" : qUnion([Q0, Q1, Q2, Q3, Q4, Q5, Q6, Q7, Q8, Q9, Q10, Q11, Q12]), "transformType" : TransformType.TRANSLATION_3D, "dx" : -975.93 * mm, "dy" : -250 * mm, "dz" : -383.36 * mm, "makeCopy" : false});
        }
    });
